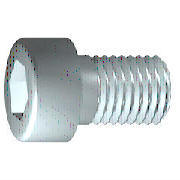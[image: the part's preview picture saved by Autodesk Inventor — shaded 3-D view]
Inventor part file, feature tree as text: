
AUTODESK INVENTOR PART (.ipt)
format: ipt  version: 2024.1 (Build 281209000, 209)  size: 195,072 bytes
history: native  units: mm (DEFAULTED — no unit token found)
features: extrude x1, plane x1, fillet x1
ambient origin geometry x7: Origin, YZ Plane, XY Plane, X Axis, Y Axis, Z Axis, Center Point
bodies: Solid1 (feature_tree), Body (feature_tree)
feature tree (3):
  extrude  "Slot"  Depth=5.0mm
  plane  "Work Plane1"
  fillet  "Fillet2"  Radius=0.24548mm
